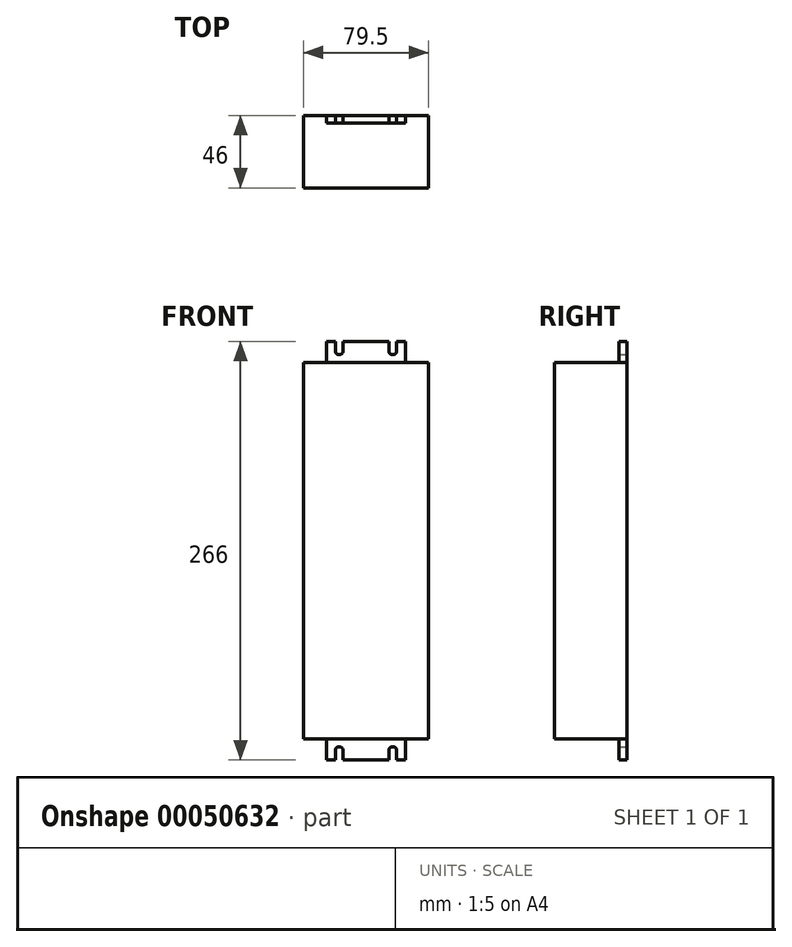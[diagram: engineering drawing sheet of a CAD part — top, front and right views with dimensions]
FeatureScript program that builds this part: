
annotation { "Feature Type Name" : "Feature", "Feature Type Description" : "" }
export const myFeature = defineFeature(function(context is Context, id is Id, definition is map)
    precondition{}
    {
        {
            var Q0;
            Q0=qCreatedBy(makeId("Front.planeOp"),FACE);
            var sketch = newSketch(context, id + "F0", { "sketchPlane" : qUnion([Q0])});
            skLineSegment(sketch, "E0", {"start": v(39.75, 0) * mm, "end": v(39.75, 119.5) * mm});
            skLineSegment(sketch, "E1", {"start": v(39.75, 119.5) * mm, "end": v(0, 119.5) * mm});
            skLineSegment(sketch, "E2", {"start": v(25, 133) * mm, "end": v(19.5, 133) * mm});
            skLineSegment(sketch, "E3", {"start": v(25, 133) * mm, "end": v(25, 119.5) * mm});
            skLineSegment(sketch, "E4", {"start": v(19.5, 133) * mm, "end": v(19.5, 126.25) * mm});
            skLineSegment(sketch, "E5", {"start": v(14.5, 126.25) * mm, "end": v(14.5, 133) * mm});
            skLineSegment(sketch, "E6.trimOffspring", {"start": v(14.5, 133) * mm, "end": v(0, 133) * mm});
            skPoint(sketch, "E7.endSnap0", {"position": v(25, 126.25) * mm});
            skArc(sketch, "E8", {"start": v(14.5, 127) * mm, "mid": v(17, 124.5) * mm, "end": v(19.5, 127) * mm});
            skArc(sketch, "E9.MirrorCS", {"start": v(-14.5, 127) * mm, "mid": v(-17, 124.5) * mm, "end": v(-19.5, 127) * mm});
            skPoint(sketch, "E10.MirrorP", {"position": v(-25, 126.25) * mm});
            skLineSegment(sketch, "E11.MirrorCS", {"start": v(-19.5, 133) * mm, "end": v(-19.5, 126.25) * mm});
            skLineSegment(sketch, "E12.MirrorCS", {"start": v(-14.5, 126.25) * mm, "end": v(-14.5, 133) * mm});
            skLineSegment(sketch, "E13.MirrorCS", {"start": v(-39.75, 0) * mm, "end": v(-39.75, 119.5) * mm});
            skLineSegment(sketch, "E14.MirrorCS", {"start": v(-14.5, 133) * mm, "end": v(0, 133) * mm});
            skLineSegment(sketch, "E15.MirrorCS", {"start": v(-39.75, 119.5) * mm, "end": v(0, 119.5) * mm});
            skLineSegment(sketch, "E16.MirrorCS", {"start": v(-25, 133) * mm, "end": v(-19.5, 133) * mm});
            skLineSegment(sketch, "E17.MirrorCS", {"start": v(-25, 133) * mm, "end": v(-25, 119.5) * mm});
            skLineSegment(sketch, "E18.MirrorCS", {"start": v(25, -133) * mm, "end": v(19.5, -133) * mm});
            skLineSegment(sketch, "E19.MirrorCS", {"start": v(-25, -133) * mm, "end": v(-19.5, -133) * mm});
            skArc(sketch, "E20.MirrorCS", {"start": v(14.5, -127) * mm, "mid": v(17, -124.5) * mm, "end": v(19.5, -127) * mm});
            skArc(sketch, "E21.MirrorCS", {"start": v(-14.5, -127) * mm, "mid": v(-17, -124.5) * mm, "end": v(-19.5, -127) * mm});
            skLineSegment(sketch, "E22.MirrorCS", {"start": v(-14.5, -133) * mm, "end": v(0, -133) * mm});
            skLineSegment(sketch, "E23.MirrorCS", {"start": v(-39.75, 0) * mm, "end": v(-39.75, -119.5) * mm});
            skLineSegment(sketch, "E24.MirrorCS", {"start": v(-14.5, -126.25) * mm, "end": v(-14.5, -133) * mm});
            skPoint(sketch, "E25.MirrorP", {"position": v(-25, -126.25) * mm});
            skLineSegment(sketch, "E26.MirrorCS", {"start": v(-19.5, -133) * mm, "end": v(-19.5, -126.25) * mm});
            skLineSegment(sketch, "E27.MirrorCS", {"start": v(39.75, -119.5) * mm, "end": v(0, -119.5) * mm});
            skLineSegment(sketch, "E28.MirrorCS", {"start": v(19.5, -133) * mm, "end": v(19.5, -126.25) * mm});
            skLineSegment(sketch, "E29.MirrorCS", {"start": v(14.5, -126.25) * mm, "end": v(14.5, -133) * mm});
            skLineSegment(sketch, "E30.MirrorCS", {"start": v(39.75, 0) * mm, "end": v(39.75, -119.5) * mm});
            skLineSegment(sketch, "E31.MirrorCS", {"start": v(-25, -133) * mm, "end": v(-25, -119.5) * mm});
            skPoint(sketch, "E32.MirrorP", {"position": v(25, -126.25) * mm});
            skLineSegment(sketch, "E33.MirrorCS", {"start": v(25, -133) * mm, "end": v(25, -119.5) * mm});
            skLineSegment(sketch, "E34.MirrorCS", {"start": v(-39.75, -119.5) * mm, "end": v(0, -119.5) * mm});
            skLineSegment(sketch, "E35.MirrorCS", {"start": v(14.5, -133) * mm, "end": v(0, -133) * mm});
            skSolve(sketch);
        }
        {
            var Q0;
            {var subQ13=sQuery(id+"F0.wireOp",EDGE,"E2");Q0=makeQuery(id+"F0.imprint","IMPRINT",FACE,{"disambiguationData":[TD([[makeQuery(id+"F0.imprint","IMPRINT",EDGE,{"derivedFrom":subQ13}),1.0]])]});}
            var Q1;
            {var subQ5=sQuery(id+"F0.wireOp",EDGE,"E18.MirrorCS");Q1=makeQuery(id+"F0.imprint","IMPRINT",FACE,{"disambiguationData":[TD([[makeQuery(id+"F0.imprint","IMPRINT",EDGE,{"derivedFrom":subQ5}),-1.0]])]});}
            extrude(context, id + "F1", {"entities" : qUnion([Q0, Q1]), "depth" : 5 * mm});
        }
        {
            var Q0;
            {var subQ13=sQuery(id+"F0.wireOp",EDGE,"E0");Q0=makeQuery(id+"F0.imprint","IMPRINT",FACE,{"disambiguationData":[TD([[makeQuery(id+"F0.imprint","IMPRINT",EDGE,{"derivedFrom":subQ13}),1.0]])]});}
            extrude(context, id + "F2", {"entities" : qUnion([Q0]), "depth" : 46 * mm});
        }
    });
